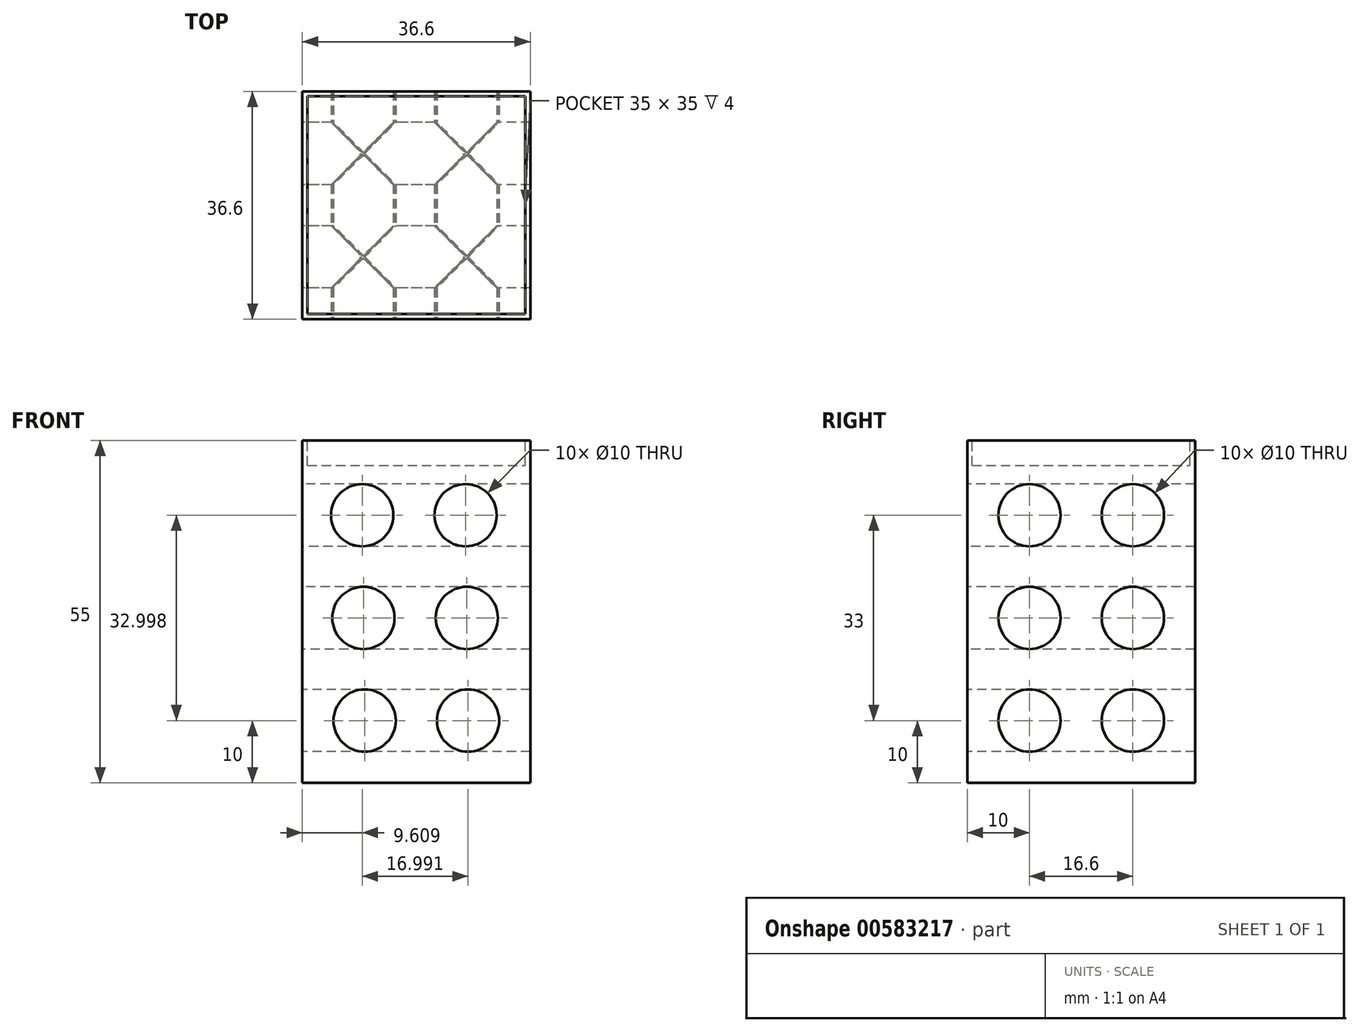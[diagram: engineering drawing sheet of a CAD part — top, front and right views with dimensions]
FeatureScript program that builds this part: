
annotation { "Feature Type Name" : "Feature", "Feature Type Description" : "" }
export const myFeature = defineFeature(function(context is Context, id is Id, definition is map)
    precondition{}
    {
        {
            var Q0;
            Q0=qCreatedBy(makeId("Top.planeOp"),FACE);
            var sketch = newSketch(context, id + "F0", { "sketchPlane" : qUnion([Q0])});
            skLineSegment(sketch, "E0.bottom", {"start": v(0, 0) * mm, "end": v(36.6, 0) * mm});
            skLineSegment(sketch, "E0.top", {"start": v(0, 36.6) * mm, "end": v(36.6, 36.6) * mm});
            skLineSegment(sketch, "E0.left", {"start": v(0, 0) * mm, "end": v(0, 36.6) * mm});
            skLineSegment(sketch, "E0.right", {"start": v(36.6, 0) * mm, "end": v(36.6, 36.6) * mm});
            skSolve(sketch);
        }
        {
            var Q0;
            Q0=makeQuery(id+"F0.imprint","IMPRINT",FACE,{"disambiguationData":[TD([[makeQuery(id+"F0.imprint","IMPRINT",EDGE,{"derivedFrom":sQuery(id+"F0.wireOp",EDGE,"E0.bottom")}),1.0]])]});
            extrude(context, id + "F1", {"entities" : qUnion([Q0]), "depth" : 55 * mm, "offsetDistance" : 25 * mm});
        }
        {
            var Q0;
            Q0=makeQuery(id+"F1.opExtrude","CAP_FACE",FACE,{"disambiguationData":[OSD([sQuery(id+"F0.wireOp",EDGE,"E0.bottom"),sQuery(id+"F0.wireOp",EDGE,"E0.top"),sQuery(id+"F0.wireOp",EDGE,"E0.left"),sQuery(id+"F0.wireOp",EDGE,"E0.right")])],"isStart":false});
            var sketch = newSketch(context, id + "F2", { "sketchPlane" : qUnion([Q0])});
            skLineSegment(sketch, "E1.bottom", {"start": v(0.8, 0.8) * mm, "end": v(35.8, 0.8) * mm});
            skLineSegment(sketch, "E1.top", {"start": v(0.8, 35.8) * mm, "end": v(35.8, 35.8) * mm});
            skLineSegment(sketch, "E1.left", {"start": v(0.8, 0.8) * mm, "end": v(0.8, 35.8) * mm});
            skLineSegment(sketch, "E1.right", {"start": v(35.8, 0.8) * mm, "end": v(35.8, 35.8) * mm});
            skSolve(sketch);
        }
        {
            var Q0;
            Q0 = qSketchRegion(id + "F2", true);
            extrude(context, id + "F3", {"entities" : qUnion([Q0]), "operationType" : NewBodyOperationType.REMOVE, "oppositeDirection" : true, "depth" : 4 * mm, "offsetDistance" : 25 * mm});
        }
        {
            var Q0;
            Q0=makeQuery(id+"F1.opExtrude","SWEPT_FACE",FACE,{"disambiguationData":[OSD([sQuery(id+"F0.wireOp",EDGE,"E0.bottom")])]});
            var sketch = newSketch(context, id + "F4", { "sketchPlane" : qUnion([Q0])});
            skLineSegment(sketch, "E2.1", {"start": v(0, 0) * mm, "end": v(36.6, 0) * mm, "construction": true});
            skLineSegment(sketch, "E3.0", {"start": v(0.8, 51) * mm, "end": v(35.8, 51) * mm, "construction": true});
            skCircle(sketch, "E4", {"center": v(10, 10) * mm, "radius": 5 * mm});
            skCircle(sketch, "E5", {"center": v(26.6, 10) * mm, "radius": 5 * mm});
            skCircle(sketch, "E6.0.1.0", {"center": v(9.8, 26.5) * mm, "radius": 5 * mm});
            skCircle(sketch, "E6.0.1.1", {"center": v(26.4, 26.5) * mm, "radius": 5 * mm});
            skCircle(sketch, "E6.0.2.0", {"center": v(9.6, 43) * mm, "radius": 5 * mm});
            skCircle(sketch, "E6.0.2.1", {"center": v(26.2, 43) * mm, "radius": 5 * mm});
            skLineSegment(sketch, "E6.direction1", {"start": v(10, 10) * mm, "end": v(46.3, 10) * mm, "construction": true});
            skLineSegment(sketch, "E6.direction2", {"start": v(10, 10) * mm, "end": v(9.8, 26.5) * mm, "construction": true});
            skSolve(sketch);
        }
        {
            var Q0;
            Q0 = qSketchRegion(id + "F4", true);
            extrude(context, id + "F5", {"entities" : qUnion([Q0]), "operationType" : NewBodyOperationType.REMOVE, "oppositeDirection" : true, "depth" : 70 * mm, "offsetDistance" : 25 * mm});
        }
        {
            var Q0;
            Q0=makeQuery(id+"F1.opExtrude","SWEPT_FACE",FACE,{"disambiguationData":[OSD([sQuery(id+"F0.wireOp",EDGE,"E0.left")])]});
            var sketch = newSketch(context, id + "F6", { "sketchPlane" : qUnion([Q0])});
            skCircle(sketch, "E7", {"center": v(-26.6, 10) * mm, "radius": 5 * mm});
            skCircle(sketch, "E8", {"center": v(-10, 10) * mm, "radius": 5 * mm});
            skCircle(sketch, "E9.0.1.0", {"center": v(-10, 26.5) * mm, "radius": 5 * mm});
            skCircle(sketch, "E9.0.1.1", {"center": v(-26.6, 26.5) * mm, "radius": 5 * mm});
            skCircle(sketch, "E9.0.2.0", {"center": v(-10, 43) * mm, "radius": 5 * mm});
            skCircle(sketch, "E9.0.2.1", {"center": v(-26.6, 43) * mm, "radius": 5 * mm});
            skLineSegment(sketch, "E9.direction1", {"start": v(-10, 10) * mm, "end": v(15, 10) * mm, "construction": true});
            skLineSegment(sketch, "E9.direction2", {"start": v(-10, 10) * mm, "end": v(-10, 26.5) * mm, "construction": true});
            skSolve(sketch);
        }
        {
            var Q0;
            Q0 = qSketchRegion(id + "F6", true);
            extrude(context, id + "F7", {"entities" : qUnion([Q0]), "operationType" : NewBodyOperationType.REMOVE, "oppositeDirection" : true, "depth" : 50 * mm, "offsetDistance" : 25 * mm});
        }
    });
